# Revit family: Faucet-Lavatory-Spout-KALLISTA-Juxtapose-P23175-1
name_source: partatom
category: Plumbing Fixtures
units: mm (PartAtom-declared; Revit-internal decimal feet)

## family parameters
Cut with Voids When Loaded = No
Host = Face
OmniClass Number = 23.31.11.00
OmniClass Title = Faucets
Part Type = Normal
Room Calculation Point = No
Round Connector Dimension = Use Diameter
Shared = No

## types (6) — shared parameters
ADA Compliant = No
Assembly Code = D2010
CW Connection = Yes
Cold Water Inlet = Cold Water Inlet
Date Modified = 11/14/2024
Default Elevation = 36"
Description = Bar Faucet
Drain Included = No
Flow Rate = 2 GPM
HW Connection = Yes
Handle Clearance = 3 1/2"
Height = 13"
Hot Water Inlet = Hot Water Inlet
Length = 5 13/16"
Manufacturer = Kallista Co.
Master Format 2014 = 22 41 39
Master Format 2014 Name = Residential Faucets, Supplies, and Trim
Material = Premium Metal Construction
Pressure = 60.00 psi
Product Documentation Link = https://resources.kohler.com
Product Name = Juxtapose
Spout Reach = 5 13/16"
URL = https://www.kallista.com
Vent Connection = No
Waste Connection = No
Waste Water Outlet = Waste Water Outlet
WaterSense Certified = No
Width = 2 1/16"

## per-type parameters (varying)
| type | Finish | Model | Product Page URL | Secondary Finish | Type |
| 2MB, VS-Stainless | Kallista-Metal-VS-Stainless | P23175-2MB-VS |  | Kallista-Metal-2MB- Brushed_Brass | 1 |
| 2MB, BL-Matte Black | Kallista-Metal-BL-Matte_Black | P23175-2MB-BL | https://www.kallista.com | Kallista-Metal-2MB- Brushed_Brass | 2 |
| AF, BAF-Brushed French Gold | Kallista-Metal-BAF-Brushed_French_Gold | P23175-AF-BAF |  | Kallista-Metal-AF-French_Gold | 3 |
| LV, BL-Matte Black | Kallista-Metal-BL-Matte_Black | P23175-LV-BL | https://www.kallista.com | Kallista-Metal-BL-Matte_Black | 4 |
| LV, CP-Chrome | Kallista-Metal-CP-Chrome | P23175-LV-CP | https://www.kallista.com | Kallista-Metal-CP-Chrome | 5 |
| SN, VS-Stainless | Kallista-Metal-VS-Stainless | P23175-SN-VS | https://www.kallista.com | Kallista-Metal-SN-Polished_Nickel | 6 |

## geometry (parser evidence)
native form markers: Sweep x6
no freeform markers — native parametric forms only
